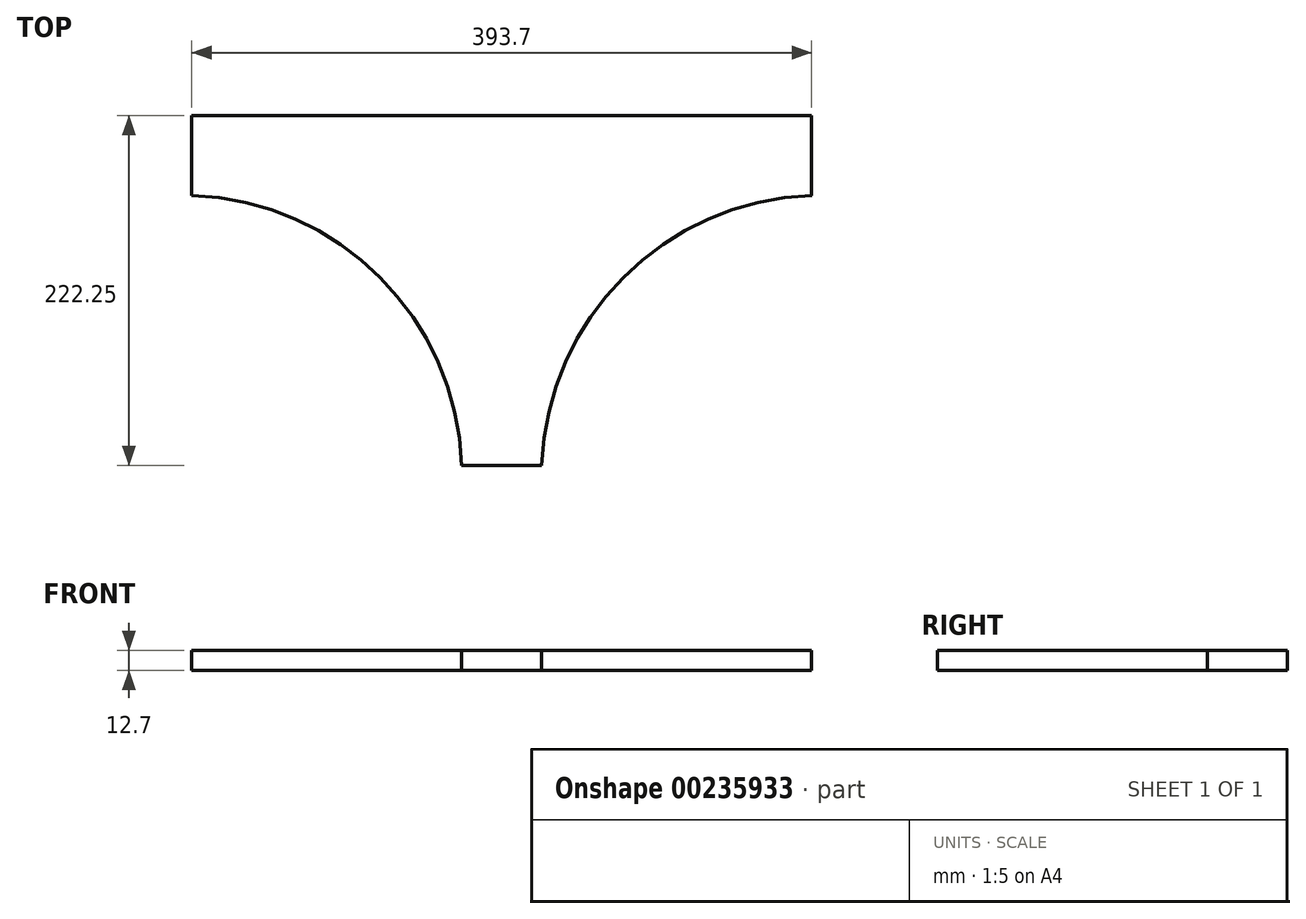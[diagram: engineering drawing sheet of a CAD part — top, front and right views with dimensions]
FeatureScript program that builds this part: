
annotation { "Feature Type Name" : "Feature", "Feature Type Description" : "" }
export const myFeature = defineFeature(function(context is Context, id is Id, definition is map)
    precondition{}
    {
        {
            var Q0;
            Q0=qCreatedBy(makeId("Top.planeOp"),FACE);
            var sketch = newSketch(context, id + "F0", { "sketchPlane" : qUnion([Q0])});
            skLineSegment(sketch, "E0", {"start": v(0, 0) * mm, "end": v(393.7, 0) * mm, "construction": true});
            skLineSegment(sketch, "E1", {"start": v(196.85, 0) * mm, "end": v(196.85, -196.85) * mm, "construction": true});
            skLineSegment(sketch, "E2", {"start": v(0, 0) * mm, "end": v(0, 25.4) * mm});
            skLineSegment(sketch, "E3.MirrorCS", {"start": v(393.7, 0) * mm, "end": v(393.7, 25.4) * mm});
            skLineSegment(sketch, "E4.MirrorCS", {"start": v(0, 0) * mm, "end": v(0, -25.4) * mm});
            skLineSegment(sketch, "E5.MirrorCS", {"start": v(393.7, 0) * mm, "end": v(393.7, -25.4) * mm});
            skLineSegment(sketch, "E6", {"start": v(196.85, -196.85) * mm, "end": v(222.25, -196.85) * mm});
            skLineSegment(sketch, "E7.MirrorCS", {"start": v(196.85, -196.85) * mm, "end": v(171.45, -196.85) * mm});
            skLineSegment(sketch, "E8", {"start": v(0, 25.4) * mm, "end": v(393.7, 25.4) * mm});
            skArc(sketch, "E9", {"start": v(171.45, -196.85) * mm, "mid": v(119.48, -77.37) * mm, "end": v(0, -25.4) * mm});
            skArc(sketch, "E10.MirrorCS", {"start": v(222.25, -196.85) * mm, "mid": v(274.22, -77.37) * mm, "end": v(393.7, -25.4) * mm});
            skSolve(sketch);
        }
        {
            var Q0;
            Q0=makeQuery(id+"F0.imprint","IMPRINT",FACE,{"disambiguationData":[TD([[makeQuery(id+"F0.imprint","IMPRINT",EDGE,{"derivedFrom":sQuery(id+"F0.wireOp",EDGE,"E2")}),-1.0]])]});
            extrude(context, id + "F1", {"entities" : qUnion([Q0]), "endBound" : BoundingType.SYMMETRIC, "depth" : 12.7 * mm});
        }
    });
